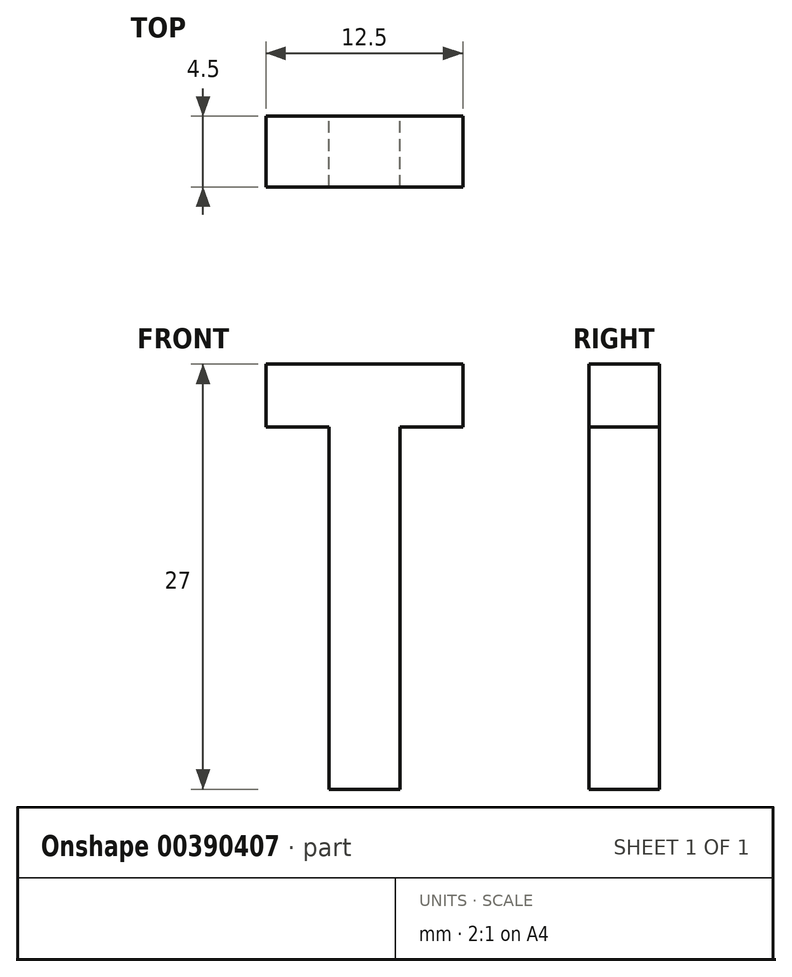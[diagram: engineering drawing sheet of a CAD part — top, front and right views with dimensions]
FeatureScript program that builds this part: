
annotation { "Feature Type Name" : "Feature", "Feature Type Description" : "" }
export const myFeature = defineFeature(function(context is Context, id is Id, definition is map)
    precondition{}
    {
        {
            var Q0;
            Q0=qCreatedBy(makeId("Front.planeOp"),FACE);
            var sketch = newSketch(context, id + "F0", { "sketchPlane" : qUnion([Q0])});
            skLineSegment(sketch, "E0", {"start": v(-6.25, 4) * mm, "end": v(-6.25, 0) * mm});
            skLineSegment(sketch, "E1", {"start": v(-6.25, 0) * mm, "end": v(-2.25, 0) * mm});
            skLineSegment(sketch, "E2", {"start": v(-2.25, 0) * mm, "end": v(-2.25, -23) * mm});
            skLineSegment(sketch, "E3", {"start": v(-2.25, -23) * mm, "end": v(2.25, -23) * mm});
            skLineSegment(sketch, "E4", {"start": v(2.25, -23) * mm, "end": v(2.25, 0) * mm});
            skLineSegment(sketch, "E5", {"start": v(2.25, 0) * mm, "end": v(6.25, 0) * mm});
            skLineSegment(sketch, "E6", {"start": v(6.25, 0) * mm, "end": v(6.25, 4) * mm});
            skLineSegment(sketch, "E7", {"start": v(6.25, 4) * mm, "end": v(-6.25, 4) * mm});
            skSolve(sketch);
        }
        {
            var Q0;
            Q0 = qSketchRegion(id + "F0", true);
            extrude(context, id + "F1", {"entities" : qUnion([Q0]), "depth" : (4.5 / 2) * mm, "hasSecondDirection" : true, "secondDirectionOppositeDirection" : true, "secondDirectionDepth" : (4.5 / 2) * mm});
        }
    });
